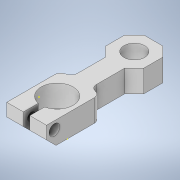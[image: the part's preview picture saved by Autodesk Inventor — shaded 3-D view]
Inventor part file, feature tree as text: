
AUTODESK INVENTOR PART (.ipt)
format: ipt  version: 2021 (Build 250183000, 183)  size: 237,568 bytes
history: native  units: in
note: dims shown in document units (in); Inventor stores cm internally (conversion verified against a paired STEP export)
features: sketch x13, extrude x6, hole x4, fillet x3, chamfer x1
ambient origin geometry x8: Origin, YZ Plane, XZ Plane, XY Plane, X Axis, Y Axis, Z Axis, Center Point
bodies: Solid1 (feature_tree)
feature tree (27):
  extrude  "Extrusion1"  Depth=0.4921in
  chamfer  "Chamfer1"  Distance=0.2756in
  extrude  "Extrusion2"  Depth=0.1181in
  extrude  "Extrusion3"  Depth=0.378in
  hole  "Hole1"  [1 undecoded]
  hole  "Hole2"  [1 undecoded]
  extrude  "Extrusion4"  Depth=0.2362in
  fillet  "Fillet1"  Radius=0.0984in
  fillet  "Fillet2"  Radius=0.0984in
  fillet  "Fillet3"  Radius=0.0984in
  sketch  "Sketch7"  dims[d19=0.1339in d20=0.2362in d21=0.248in d22=0.0787in d23=90.0deg d24=0.2362in d25=0.0in d26=0.0984in d27=0.0984in]
  sketch  "Sketch8"  dims[d28=0.0968in d29=0.2362in d30=0.248in d31=0.0787in d32=90.0deg d33=0.2362in d34=0.0in d35=0.0984in d36=0.0984in]
  extrude  "Extrusion5"  Depth=0.2756in
  extrude  "Extrusion6"  Depth=0.128in TaperAngle=0.0deg
  sketch  "Sketch11"  dims[d48=0.0787in d49=0.0787in]
  hole  "Hole3"  [1 undecoded]
  hole  "Hole4"  [1 undecoded]
  sketch  "Sketch1"  dims[d0=0.6693in d1=0.4921in d2=0.2756in d3=0.0in]
  sketch  "Sketch2"  dims[d4=0.1181in d5=0.125in d6=45.0deg d7=0.3957in]
  sketch  "Sketch3"  dims[d8=0.2461in d9=0.378in]
  sketch  "Sketch4"  dims[d10=0.3in d11=0.0in d14=0.3in d15=0.0in]
  sketch  "Sketch5"  dims[d16=0.0787in d17=0.4921in]
  sketch  "Sketch6"  dims[d18=0.2067in]
  sketch  "Sketch9"  dims[d40=0.2362in d41=0.2756in]
  sketch  "Sketch10"  dims[d42=0.128in d43=0.4272in d44=0.0in]
  sketch  "Sketch12"  dims[d50=0.0787in d54=0.2756in d55=0.0in]
  sketch  "Sketch13"  dims[d76=0.2559in d77=0.2362in d78=0.2362in d79=0.2756in d80=0.0in d89=0.0968in d90=0.0787in d91=0.1575in d92=0.0787in d93=90.0deg d94=0.0787in d95=0.0in d110=0.2362in d111=0.2362in d112=0.2362in d113=0.2362in d114=45.0deg d115=135.0deg d116=45.0deg d117=45.0deg d118=45.0deg d119=0.1181in d120=0.1181in d121=0.4724in d122=0.2756in d123=0.167in d124=0.0968in d125=0.0787in d126=0.1575in d127=0.0787in d128=90.0deg d129=0.0787in d130=0.0in d56=0.0197in d57=0.0344in d131=0.0025in d132=0.0295in d133=0.0148in]
note: 4 required parameter values undecoded (feature->parameter linkage not recoverable at this tier; creation-order binding heuristic only, values carry confidence <= 0.55)
